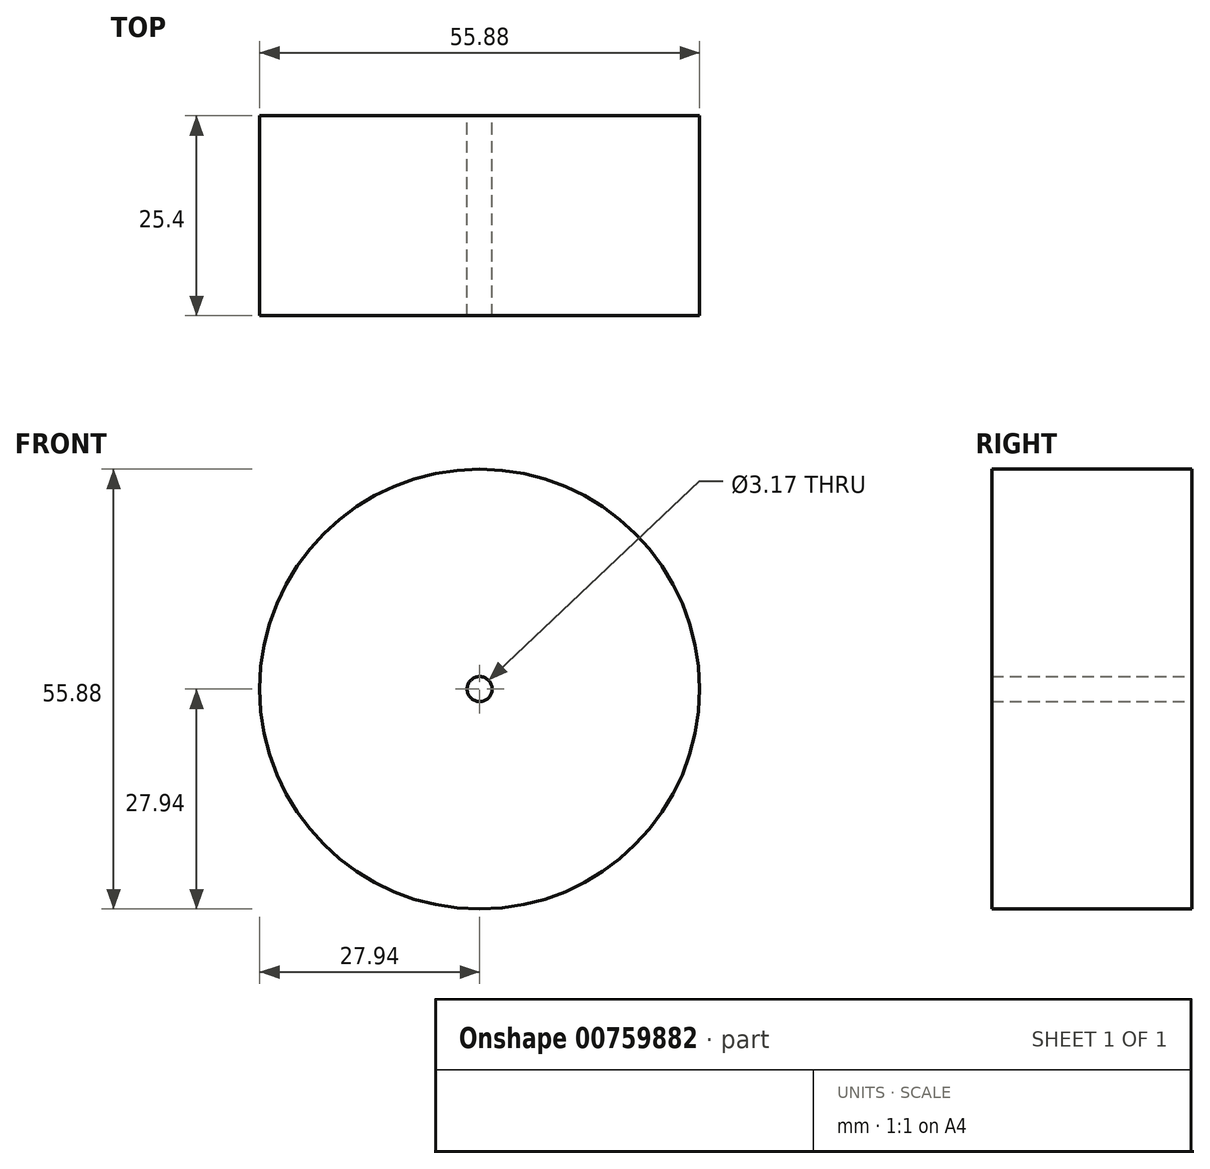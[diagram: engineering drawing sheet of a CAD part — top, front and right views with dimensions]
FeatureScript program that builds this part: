
annotation { "Feature Type Name" : "Feature", "Feature Type Description" : "" }
export const myFeature = defineFeature(function(context is Context, id is Id, definition is map)
    precondition{}
    {
        {
            var Q0;
            Q0=qCreatedBy(makeId("Front.planeOp"),FACE);
            var sketch = newSketch(context, id + "F0", { "sketchPlane" : qUnion([Q0])});
            skCircle(sketch, "E0", {"center": v(0, 0) * mm, "radius": 27.94 * mm});
            skCircle(sketch, "E1", {"center": v(0, 0) * mm, "radius": 1.59 * mm});
            skSolve(sketch);
        }
        {
            var Q0;
            Q0=makeQuery(id+"F0.imprint","IMPRINT",FACE,{"disambiguationData":[TD([[makeQuery(id+"F0.imprint","IMPRINT",EDGE,{"derivedFrom":sQuery(id+"F0.wireOp",EDGE,"E0")}),1.0]])]});
            extrude(context, id + "F1", {"entities" : qUnion([Q0]), "depth" : 25.4 * mm, "offsetDistance" : 25.4 * mm});
        }
    });
